# Revit family: METEOR_Atria II 10_REVIT_File (Standard)
name_source: partatom
category: Lighting Fixtures
revit_build: Autodesk Revit 2017 (Build: 20160225_1515(x64)
units: mm (PartAtom-declared; Revit-internal decimal feet)

## family parameters
Always vertical = Yes
Cut with Voids When Loaded = No
Host = Ceiling
Light Source = Yes
OmniClass Number = 23.80.70.11
OmniClass Title = Luminaries for Internal Lighting
Part Type = Normal
Room Calculation Point = No
Round Connector Dimension = Use Diameter
Shared = No

## types (80) — shared parameters
Apparent Load = 120 VA
Color Filter = 16777215
Dimming Lamp Color Temperature Shift = <None>
StemLength = -1' - 0"
Tilt Angle = 90.00°

## per-type parameters (varying)
| type | Photometric Web File | Wattage Comments |
| ASII10-80W-278-30D | ASII10-80-278-XXX-XXX-30-XXX.IES | 80W |
| ASII10-80W-278-45D | ASII10-80-278-XXX-XXX-45-XXX.IES | 80W |
| ASII10-80W-278-55D | ASII10-80-278-XXX-XXX-55-XXX.IES | 80W |
| ASII10-80W-308-55D | ASII10-80-308-XXX-XXX-55-XXX.IES | 80W |
| ASII10-80W-308-45D | ASII10-80-308-XXX-XXX-45-XXX.IES | 80W |
| ASII10-80W-308-30D | ASII10-80-308-XXX-XXX-30-XXX.IES | 80W |
| ASII10-80W-358-45D | ASII10-80-358-XXX-XXX-45-XXX.IES | 80W |
| ASII10-80W-358-30D | ASII10-80-358-XXX-XXX-30-XXX.IES | 80W |
| ASII10-80W-358-55D | ASII10-80-358-XXX-XXX-55-XXX.IES | 80W |
| ASII10-80W-408-55D | ASII10-80-408-XXX-XXX-55-XXX.IES | 80W |
| ASII10-80W-408-45D | ASII10-80-408-XXX-XXX-45-XXX.IES | 80W |
| ASII10-80W-408-30D | ASII10-110-408-XXX-XXX-30-XXX.IES | 80W |
| ASII10-80W-278-WD | ASII10-80-278-XXX-XXX-WD-XXX.ies | 80W |
| ASII10-80W-308-WD | ASII10-80-308-XXX-XXX-WD-XXX.ies | 80W |
| ASII10-80W-358-WD | ASII10-80-358-XXX-XXX-WD-XXX.ies | 80W |
| ASII10-80W-408-WD | ASII10-110-408-XXX-XXX-WD-XXX.ies | 80W |
| ASII10-110W-278-30D | ASII10-110-278-XXX-XXX-30-XXX.IES | 110W |
| ASII10-110W-278-45D | ASII10-110-278-XXX-XXX-45-XXX.IES | 110W |
| ASII10-110W-278-55D | ASII10-110-278-XXX-XXX-55-XXX.IES | 110W |
| ASII10-110W-308-55D | ASII10-110-308-XXX-XXX-55-XXX.IES | 110W |
| ASII10-110W-308-45D | ASII10-110-308-XXX-XXX-45-XXX.IES | 110W |
| ASII10-110W-308-30D | ASII10-110-308-XXX-XXX-30-XXX.IES | 110W |
| ASII10-110W-358-45D | ASII10-110-358-XXX-XXX-45-XXX.IES | 110W |
| ASII10-110W-358-30D | ASII10-110-358-XXX-XXX-30-XXX.IES | 110W |
| ASII10-110W-358-55D | ASII10-110-358-XXX-XXX-55-XXX.IES | 110W |
| ASII10-110W-408-55D | ASII10-110-408-XXX-XXX-55-XXX.IES | 110W |
| ASII10-110W-408-45D | ASII10-110-408-XXX-XXX-45-XXX.IES | 110W |
| ASII10-110W-408-30D | ASII10-110-408-XXX-XXX-30-XXX.IES | 110W |
| ASII10-110W-358-WD | ASII10-110-358-XXX-XXX-WD-XXX.ies | 110W |
| ASII10-110W-308-WD | ASII10-110-308-XXX-XXX-WD-XXX.ies | 110W |
| ASII10-110W-278-WD | ASII10-110-278-XXX-XXX-WD-XXX.ies | 110W |
| ASII10-110W-408-WD | ASII10-110-408-XXX-XXX-WD-XXX.ies | 110W |
| ASII10-140W-278-45D | ASII10-140-278-XXX-XXX-45-XXX.IES | 140W |
| ASII10-140W-278-55D | ASII10-140-278-XXX-XXX-55-XXX.IES | 140W |
| ASII10-140W-308-30D | ASII10-140-308-XXX-XXX-30-XXX.IES | 140W |
| ASII10-140W-358-30D | ASII10-140-358-XXX-XXX-30-XXX.IES | 140W |
| ASII10-140W-308-55D | ASII10-140-308-XXX-XXX-55-XXX.IES | 140W |
| ASII10-140W-308-45D | ASII10-80-308-XXX-XXX-45-XXX.IES | 140W |
| ASII10-140W-358-55D | ASII10-140-358-XXX-XXX-55-XXX.IES | 140W |
| ASII10-140W-358-45D | ASII10-140-358-XXX-XXX-45-XXX.IES | 140W |
| ASII10-140W-408-30D | ASII10-140-408-XXX-XXX-30-XXX.IES | 140W |
| ASII10-140W-408-55D | ASII10-140-408-XXX-XXX-55-XXX.IES | 140W |
| ASII10-140W-408-45D | ASII10-140-408-XXX-XXX-45-XXX.IES | 140W |
| ASII10-140W-278-30D | ASII10-140-278-XXX-XXX-30-XXX.IES | 140W |
| ASII10-140W-278-WD | ASII10-140-278-XXX-XXX-WD-XXX.ies | 140W |
| ASII10-140W-308-WD | ASII10-140-308-XXX-XXX-WD-XXX.ies | 140W |
| ASII10-140W-358-WD | ASII10-140-358-XXX-XXX-WD-XXX.ies | 140W |
| ASII10-140W-408-WD | ASII10-140-408-XXX-XXX-WD-XXX.ies | 140W |
| ASII10-180W-278-30D | ASII10-180-278-XXX-XXX-30-XXX.IES | 180W |
| ASII10-180W-278-45D | ASII10-180-278-XXX-XXX-45-XXX.IES | 180W |
| ASII10-180W-278-55D | ASII10-180-278-XXX-XXX-55-XXX.IES | 180W |
| ASII10-180W-308-55D | ASII10-180-308-XXX-XXX-55-XXX.IES | 180W |
| ASII10-180W-308-45D | ASII10-180-308-XXX-XXX-45-XXX.IES | 180W |
| ASII10-180W-308-30D | ASII10-140-308-XXX-XXX-30-XXX.IES | 180W |
| ASII10-180W-358-45D | ASII10-180-358-XXX-XXX-45-XXX.IES | 180W |
| ASII10-180W-358-30D | ASII10-180-358-XXX-XXX-30-XXX.IES | 180W |
| ASII10-180W-358-55D | ASII10-180-358-XXX-XXX-55-XXX.IES | 180W |
| ASII10-180W-408-55D | ASII10-180-408-XXX-XXX-55-XXX.IES | 180W |
| ASII10-180W-408-45D | ASII10-180-408-XXX-XXX-45-XXX.IES | 180W |
| ASII10-180W-408-30D | ASII10-180-408-XXX-XXX-30-XXX.IES | 180W |
| ASII10-180W-278-WD | ASII10-180-278-XXX-XXX-WD-XXX.ies | 180W |
| ASII10-180W-308-WD | ASII10-180-308-XXX-XXX-WD-XXX.ies | 180W |
| ASII10-180W-358-WD | ASII10-180-358-XXX-XXX-WD-XXX.ies | 180W |
| ASII10-180W-408-WD | ASII10-180-408-XXX-XXX-WD-XXX.ies | 180W |
| ASII10-220W-278-30D | ASII10-220-278-XXX-XXX-30-XXX.IES | 220W |
| ASII10-220W-278-45D | ASII10-220-278-XXX-XXX-45-XXX.IES | 220W |
| ASII10-220W-278-55D | ASII10-220-278-XXX-XXX-55-XXX.IES | 220W |
| ASII10-220W-308-55D | ASII10-220-308-XXX-XXX-55-XXX.IES | 220W |
| ASII10-220W-308-45D | ASII10-220-308-XXX-XXX-45-XXX.IES | 220W |
| ASII10-220W-308-30D | ASII10-220-308-XXX-XXX-30-XXX.IES | 220W |
| ASII10-220W-358-45D | ASII10-220-358-XXX-XXX-45-XXX.IES | 220W |
| ASII10-220W-358-30D | ASII10-220-358-XXX-XXX-30-XXX.IES | 220W |
| ASII10-220W-358-55D | ASII10-220-358-XXX-XXX-55-XXX.IES | 220W |
| ASII10-220W-408-55D | ASII10-220-408-XXX-XXX-55-XXX.IES | 220W |
| ASII10-220W-408-45D | ASII10-220-408-XXX-XXX-45-XXX.IES | 220W |
| ASII10-220W-408-30D | ASII10-220-408-XXX-XXX-30-XXX.IES | 220W |
| ASII10-220W-278-WD | ASII10-220-278-XXX-XXX-WD-XXX.ies | 220W |
| ASII10-220W-308-WD | ASII10-220-308-XXX-XXX-WD-XXX.ies | 220W |
| ASII10-220W-358-WD | ASII10-220-358-XXX-XXX-WD-XXX.ies | 220W |
| ASII10-220W-408-WD | ASII10-220-408-XXX-XXX-WD-XXX.ies | 220W |

## geometry (parser evidence)
native form markers: Sweep x3
no freeform markers — native parametric forms only
